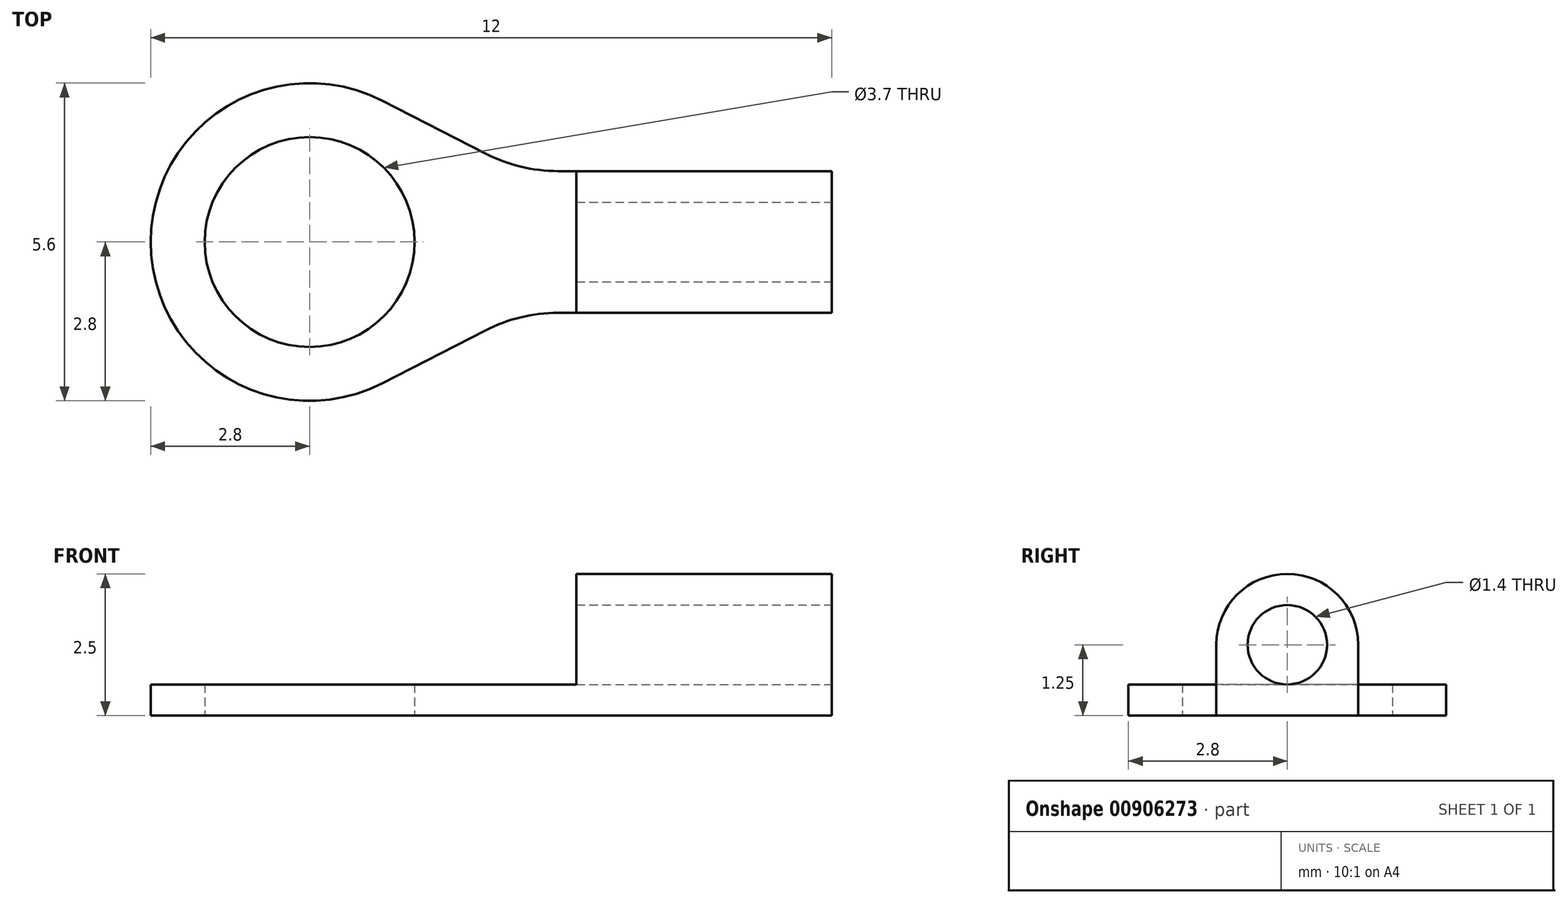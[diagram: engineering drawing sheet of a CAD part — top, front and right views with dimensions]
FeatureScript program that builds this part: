
annotation { "Feature Type Name" : "Feature", "Feature Type Description" : "" }
export const myFeature = defineFeature(function(context is Context, id is Id, definition is map)
    precondition{}
    {
        {
            var Q0;
            Q0=qCreatedBy(makeId("Top.planeOp"),FACE);
            var sketch = newSketch(context, id + "F0", { "sketchPlane" : qUnion([Q0])});
            skLineSegment(sketch, "E0", {"start": v(12, 1.55) * mm, "end": v(12, 4.05) * mm});
            skLineSegment(sketch, "E1", {"start": v(0, 2.8) * mm, "end": v(0, 2.8) * mm});
            skPoint(sketch, "E2.visualSharp", {"position": v(0, 5.6) * mm});
            skArc(sketch, "E2.filletArc", {"start": v(2.8, 5.6) * mm, "mid": v(0.82, 4.78) * mm, "end": v(0, 2.8) * mm});
            skPoint(sketch, "E3.newPointB", {"position": v(-0.5, 0) * mm});
            skArc(sketch, "E3.filletArc", {"start": v(0, 2.8) * mm, "mid": v(0.82, 0.82) * mm, "end": v(2.8, 0) * mm});
            skLineSegment(sketch, "E4.0", {"start": v(6.5, 1.47) * mm, "end": v(6.5, 1.55) * mm});
            skLineSegment(sketch, "E5.0", {"start": v(2.8, 0) * mm, "end": v(2.8, 5.6) * mm});
            skArc(sketch, "E6", {"start": v(4.08, 5.3) * mm, "mid": v(0, 2.8) * mm, "end": v(4.08, 0.3) * mm});
            skCircle(sketch, "E7", {"center": v(2.8, 2.8) * mm, "radius": 1.85 * mm});
            skLineSegment(sketch, "E8.0", {"start": v(12, 4.05) * mm, "end": v(7.18, 4.05) * mm});
            skLineSegment(sketch, "E9.0", {"start": v(12, 1.55) * mm, "end": v(7.18, 1.55) * mm});
            skLineSegment(sketch, "E10", {"start": v(5.9, 4.36) * mm, "end": v(4.08, 5.3) * mm});
            skLineSegment(sketch, "E11", {"start": v(5.9, 1.24) * mm, "end": v(4.08, 0.3) * mm});
            skPoint(sketch, "E12.visualSharp", {"position": v(6.5, 4.05) * mm});
            skArc(sketch, "E12.filletArc", {"start": v(5.9, 4.36) * mm, "mid": v(6.52, 4.13) * mm, "end": v(7.18, 4.05) * mm});
            skPoint(sketch, "E13.visualSharp", {"position": v(6.5, 1.55) * mm});
            skArc(sketch, "E13.filletArc", {"start": v(7.18, 1.55) * mm, "mid": v(6.52, 1.47) * mm, "end": v(5.9, 1.24) * mm});
            skPoint(sketch, "E14.orphan", {"position": v(12, 0) * mm});
            skPoint(sketch, "E15.end.orphan", {"position": v(6.5, 0) * mm});
            skPoint(sketch, "E16.orphan", {"position": v(12, 5.6) * mm});
            skPoint(sketch, "E17.start.orphan", {"position": v(6.5, 5.6) * mm});
            skLineSegment(sketch, "E18.trimOffspring", {"start": v(6.5, 4.05) * mm, "end": v(6.5, 4.13) * mm});
            skPoint(sketch, "E19.end.orphan", {"position": v(6.5, 2.8) * mm});
            skPoint(sketch, "E19.start.orphan", {"position": v(12, 2.8) * mm});
            skSolve(sketch);
        }
        {
            var Q0;
            Q0 = qSketchRegion(id + "F0", true);
            extrude(context, id + "F1", {"entities" : qUnion([Q0]), "depth" : 0.55 * mm, "offsetDistance" : 25 * mm});
        }
        {
            var Q0;
            Q0=makeQuery(id+"F1.opExtrude","CAP_FACE",FACE,{"disambiguationData":[OSD([sQuery(id+"F0.wireOp",EDGE,"E0"),sQuery(id+"F0.wireOp",EDGE,"E6"),sQuery(id+"F0.wireOp",EDGE,"E7"),sQuery(id+"F0.wireOp",EDGE,"E8.0"),sQuery(id+"F0.wireOp",EDGE,"E9.0"),sQuery(id+"F0.wireOp",EDGE,"E10"),sQuery(id+"F0.wireOp",EDGE,"E11"),sQuery(id+"F0.wireOp",EDGE,"E12.filletArc"),sQuery(id+"F0.wireOp",EDGE,"E13.filletArc")])],"isStart":false});
            var sketch = newSketch(context, id + "F2", { "sketchPlane" : qUnion([Q0])});
            skLineSegment(sketch, "E20.bottom", {"start": v(12, 4.05) * mm, "end": v(7.5, 4.05) * mm});
            skLineSegment(sketch, "E20.top", {"start": v(12, 1.55) * mm, "end": v(7.5, 1.55) * mm});
            skLineSegment(sketch, "E20.left", {"start": v(12, 4.05) * mm, "end": v(12, 1.55) * mm});
            skLineSegment(sketch, "E20.right", {"start": v(7.5, 4.05) * mm, "end": v(7.5, 1.55) * mm});
            skSolve(sketch);
        }
        {
            var Q0;
            Q0 = qSketchRegion(id + "F2", true);
            extrude(context, id + "F3", {"entities" : qUnion([Q0]), "operationType" : NewBodyOperationType.ADD, "depth" : 1.95 * mm, "offsetDistance" : 25 * mm});
        }
        {
            var Q0;
            Q0=makeQuery(id+"F3.opExtrude","CAP_EDGE",EDGE,{"disambiguationData":[OSD([sQuery(id+"F2.wireOp",EDGE,"E20.bottom")])],"isStart":false});
            var Q1;
            Q1=makeQuery(id+"F3.opExtrude","CAP_EDGE",EDGE,{"disambiguationData":[OSD([sQuery(id+"F2.wireOp",EDGE,"E20.top")])],"isStart":false});
            fillet(context, id + "F4", {"entities" : qUnion([Q0, Q1]), "radius" : 1.25 * mm, "tangentPropagation" : true, "allowEdgeOverflow" : false});
        }
        {
            var Q0;
            Q0=makeQuery(id+"F3.boolean.opBoolean","MERGE",FACE,{"derivedFrom":[makeQuery(id+"F1.opExtrude","SWEPT_FACE",FACE,{"disambiguationData":[OSD([sQuery(id+"F0.wireOp",EDGE,"E0")])]}),makeQuery(id+"F3.opExtrude","SWEPT_FACE",FACE,{"disambiguationData":[OSD([sQuery(id+"F2.wireOp",EDGE,"E20.left")])]})]});
            var sketch = newSketch(context, id + "F5", { "sketchPlane" : qUnion([Q0])});
            skCircle(sketch, "E21", {"center": v(2.8, 1.25) * mm, "radius": 0.7 * mm});
            skSolve(sketch);
        }
        {
            var Q0;
            Q0=makeQuery(id+"F5.imprint","IMPRINT",FACE,{"disambiguationData":[TD([[makeQuery(id+"F5.imprint","IMPRINT",EDGE,{"derivedFrom":sQuery(id+"F5.wireOp",EDGE,"E21")}),1.0]])]});
            extrude(context, id + "F6", {"entities" : qUnion([Q0]), "operationType" : NewBodyOperationType.REMOVE, "oppositeDirection" : true, "depth" : 25 * mm, "offsetDistance" : 25 * mm});
        }
    });
